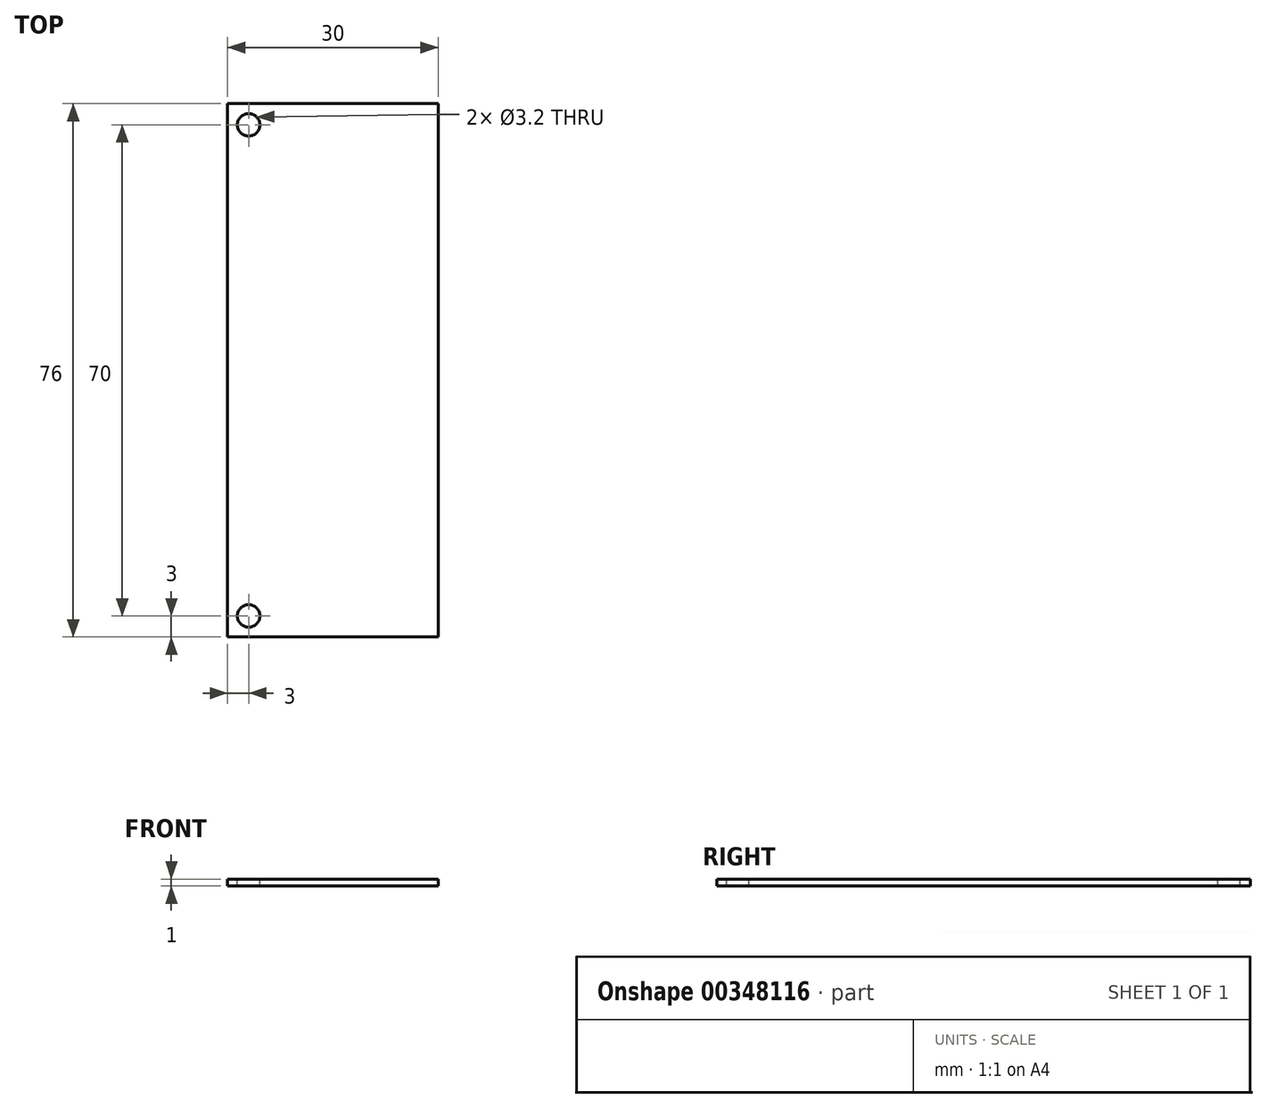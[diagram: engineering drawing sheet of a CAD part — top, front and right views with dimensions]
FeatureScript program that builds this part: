
annotation { "Feature Type Name" : "Feature", "Feature Type Description" : "" }
export const myFeature = defineFeature(function(context is Context, id is Id, definition is map)
    precondition{}
    {
        {
            var Q0;
            Q0=qCreatedBy(makeId("Top.planeOp"),FACE);
            var sketch = newSketch(context, id + "F0", { "sketchPlane" : qUnion([Q0])});
            skLineSegment(sketch, "E0.bottom", {"start": v(0, 0) * mm, "end": v(30, 0) * mm});
            skLineSegment(sketch, "E0.top", {"start": v(0, 76) * mm, "end": v(30, 76) * mm});
            skLineSegment(sketch, "E0.left", {"start": v(0, 0) * mm, "end": v(0, 76) * mm});
            skLineSegment(sketch, "E0.right", {"start": v(30, 0) * mm, "end": v(30, 76) * mm});
            skSolve(sketch);
        }
        {
            var Q0;
            Q0=makeQuery(id+"F0.imprint","IMPRINT",FACE,{"disambiguationData":[TD([[makeQuery(id+"F0.imprint","IMPRINT",EDGE,{"derivedFrom":sQuery(id+"F0.wireOp",EDGE,"E0.bottom")}),1.0]])]});
            extrude(context, id + "F1", {"entities" : qUnion([Q0]), "depth" : 1 * mm});
        }
        {
            var Q0;
            Q0=makeQuery(id+"F1.opExtrude","CAP_FACE",FACE,{"disambiguationData":[OSD([sQuery(id+"F0.wireOp",EDGE,"E0.bottom"),sQuery(id+"F0.wireOp",EDGE,"E0.top"),sQuery(id+"F0.wireOp",EDGE,"E0.left"),sQuery(id+"F0.wireOp",EDGE,"E0.right")])],"isStart":false});
            var sketch = newSketch(context, id + "F2", { "sketchPlane" : qUnion([Q0])});
            skCircle(sketch, "E1", {"center": v(3, 3) * mm, "radius": 1.6 * mm});
            skSolve(sketch);
        }
        {
            var Q0;
            Q0=makeQuery(id+"F2.imprint","IMPRINT",FACE,{"disambiguationData":[TD([[makeQuery(id+"F2.imprint","IMPRINT",EDGE,{"derivedFrom":sQuery(id+"F2.wireOp",EDGE,"E1")}),-1.0]])]});
            var sketch = newSketch(context, id + "F3", { "sketchPlane" : qUnion([Q0])});
            skCircle(sketch, "E2", {"center": v(3, 73) * mm, "radius": 1.6 * mm});
            skSolve(sketch);
        }
        {
            var Q0;
            Q0=makeQuery(id+"F2.imprint","IMPRINT",FACE,{"disambiguationData":[TD([[makeQuery(id+"F2.imprint","IMPRINT",EDGE,{"derivedFrom":sQuery(id+"F2.wireOp",EDGE,"E1")}),1.0]])]});
            extrude(context, id + "F4", {"entities" : qUnion([Q0]), "operationType" : NewBodyOperationType.REMOVE, "oppositeDirection" : true, "depth" : 25 * mm});
        }
        {
            var Q0;
            Q0=makeQuery(id+"F3.imprint","IMPRINT",FACE,{"disambiguationData":[TD([[makeQuery(id+"F3.imprint","IMPRINT",EDGE,{"derivedFrom":sQuery(id+"F3.wireOp",EDGE,"E2")}),1.0]])]});
            extrude(context, id + "F5", {"entities" : qUnion([Q0]), "operationType" : NewBodyOperationType.REMOVE, "oppositeDirection" : true, "depth" : 25 * mm});
        }
    });
